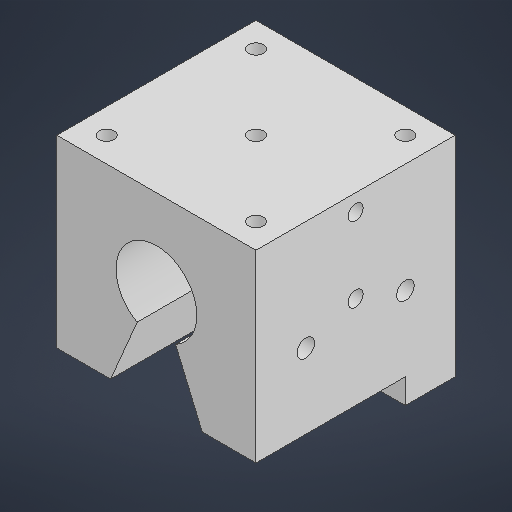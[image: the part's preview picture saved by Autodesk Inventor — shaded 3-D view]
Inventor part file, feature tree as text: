
AUTODESK INVENTOR PART (.ipt)
format: ipt  version: 2025.1 (Build 291241000, 241)  size: 405,504 bytes
history: native  units: in
note: dims shown in document units (in); Inventor stores cm internally (conversion verified against a paired STEP export)
features: extrude x5, sketch x3, projected_geometry x2, mirror x1
ambient origin geometry x8: Origin, YZ Plane, XZ Plane, XY Plane, X Axis, Y Axis, Z Axis, Center Point
bodies: Solid1 (feature_tree)
feature tree (11):
  sketch  "Sketch1"  dims[d0=0.6378in d2=0.1969in d5=0.3031in d10=1.1811in d11=0.0in]
  extrude  "Extrusion1"  Depth=1.1811in TaperAngle=0.0deg
  extrude  "Extrusion2"  Depth=1.1811in
  sketch  "Sketch6"  dims[d12=0.3937in d13=0.0in d69=1.1811in d70=0.1181in]
  extrude  "Extrusion8"  Depth=0.7874in
  extrude  "Extrusion9"  Depth=0.1969in TaperAngle=0.0deg
  extrude  "Extrusion12"  Depth=1.6535in
  mirror  "Mirror1"
  projected_geometry  "Projected Loop1"
  sketch  "Sketch8"  dims[d71=0.1969in d72=0.0in d73=0.1181in d74=0.1969in d75=0.0in d91=1.6535in d97=0.1378in d98=0.1378in d99=0.1969in d100=0.0in d102=0.7756in d103=0.7244in d104=1.5748in d105=0.7874in d106=0.7874in d107=0.7874in d108=0.5906in d109=0.7874in d110=0.1181in d25=0.0197in d26=0.0344in d27=0.0197in d28=0.0344in]
  projected_geometry  "Projected Loop3"
